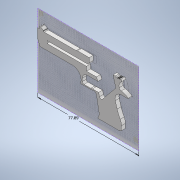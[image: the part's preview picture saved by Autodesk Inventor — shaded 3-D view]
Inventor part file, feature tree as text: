
AUTODESK INVENTOR PART (.ipt)
format: ipt  version: 2022 (Build 260153000, 153)  size: 1,788,416 bytes
history: native  units: in
note: dims shown in document units (in); Inventor stores cm internally (conversion verified against a paired STEP export)
features: other x8, reference x5, sketch x4, sheet_metal_op x3
ambient origin geometry x8: Origin, YZ Plane, XZ Plane, XY Plane, X Axis, Y Axis, Z Axis, Center Point
bodies: Solid1 (feature_tree)
feature tree (20):
  sketch  "Sketch1"  dims[d5=3.0666in]
  sheet_metal_op  "Face1"
  sheet_metal_op  "Face2"
  other  "Image1"
  sketch  "Sketch2"  dims[d16=0.12in]
  reference  "Reference6"
  other  "Plate1"
  sketch  "Sketch3"  dims[d18=0.12in]
  other  "Plate2"
  sheet_metal_op  "Bend1"
  sketch  "Sketch4"  dims[d19=0.12in d20=0.06in d21=0.24in d22=0.12in d23=0.12in d24=0.0in]
  reference  "Reference8"
  reference  "Reference9"
  reference  "Reference10"
  reference  "Reference11"
  other  "Cut1"
  parser-record x1  (decoder bookkeeping rows leaked as tree rows — omitted from the tree; the rows remain in map.json)
  other  "Assembly1.iam"
  other  "sheetmettaal_2:1"
  other  "sheetmettaal:2"
note: 1 file-system path scrubbed to <path> (originals preserved in map.json)
